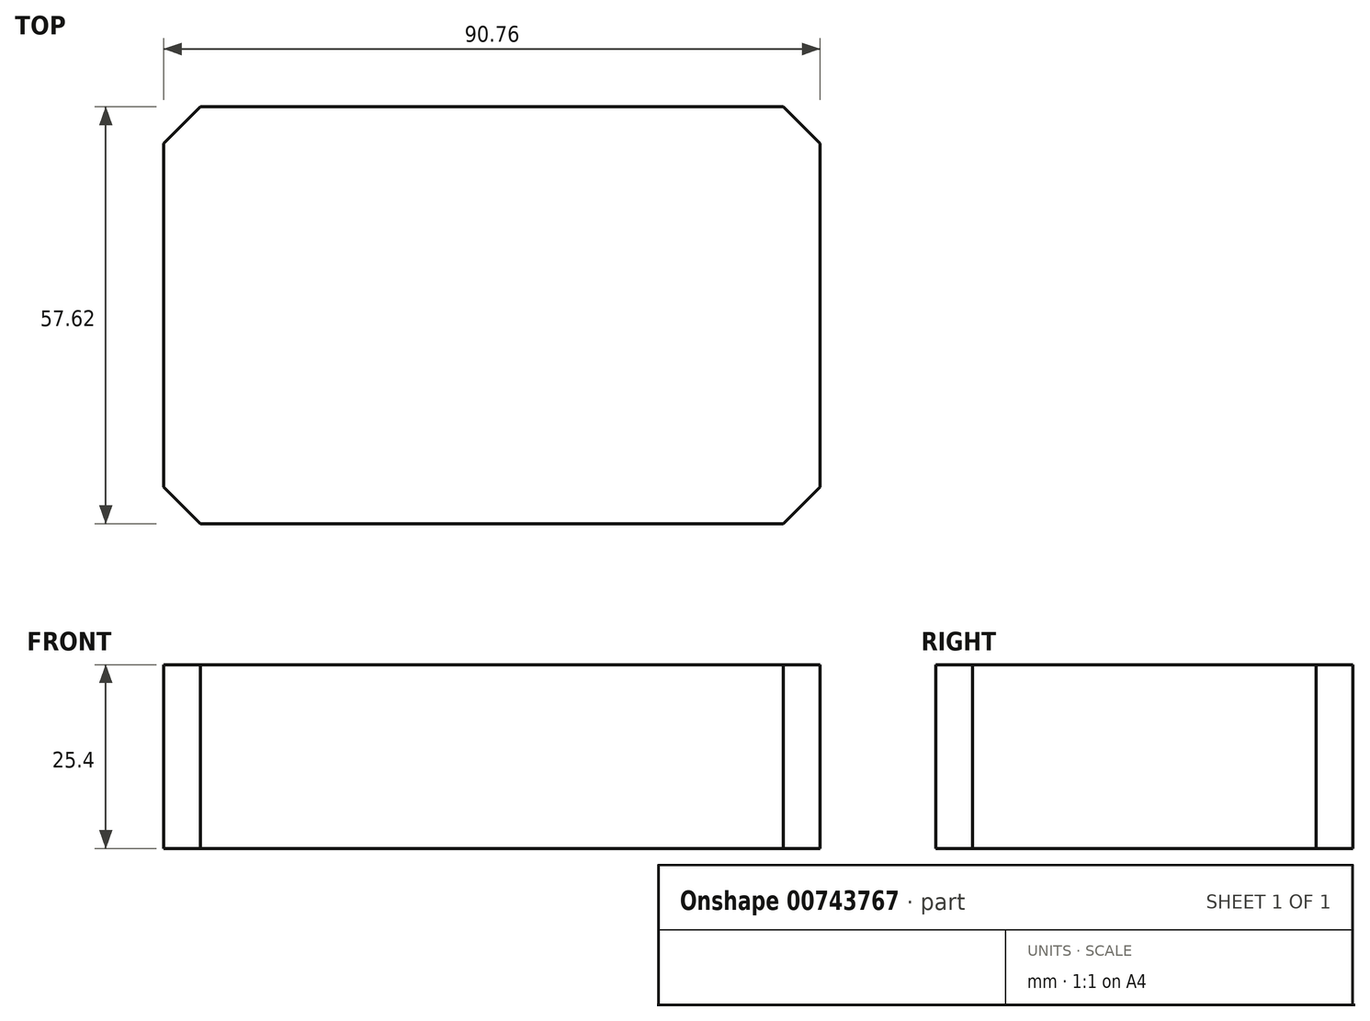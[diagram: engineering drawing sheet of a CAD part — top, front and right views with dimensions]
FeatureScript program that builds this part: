
annotation { "Feature Type Name" : "Feature", "Feature Type Description" : "" }
export const myFeature = defineFeature(function(context is Context, id is Id, definition is map)
    precondition{}
    {
        {
            var Q0;
            Q0=qCreatedBy(makeId("Top.planeOp"),FACE);
            var sketch = newSketch(context, id + "F0", { "sketchPlane" : qUnion([Q0])});
            skLineSegment(sketch, "E0.bottom", {"start": v(-45.38, 28.81) * mm, "end": v(45.38, 28.81) * mm});
            skLineSegment(sketch, "E0.top", {"start": v(-45.38, -28.81) * mm, "end": v(45.38, -28.81) * mm});
            skLineSegment(sketch, "E0.left", {"start": v(-45.38, 28.81) * mm, "end": v(-45.38, -28.81) * mm});
            skLineSegment(sketch, "E0.right", {"start": v(45.38, 28.81) * mm, "end": v(45.38, -28.81) * mm});
            skPoint(sketch, "E0.middle", {"position": v(0, 0) * mm});
            skSolve(sketch);
        }
        {
            var Q0;
            Q0=makeQuery(id+"F0.imprint","IMPRINT",FACE,{"disambiguationData":[TD([[makeQuery(id+"F0.imprint","IMPRINT",EDGE,{"derivedFrom":sQuery(id+"F0.wireOp",EDGE,"E0.bottom")}),-1.0]])]});
            extrude(context, id + "F1", {"entities" : qUnion([Q0]), "depth" : 25.4 * mm, "offsetDistance" : 25.4 * mm});
        }
        {
            var Q0;
            Q0=makeQuery(id+"F1.opExtrude","SWEPT_EDGE",EDGE,{"disambiguationData":[OSD([sQuery(id+"F0.wireOp",EDGE,"E0.top"),sQuery(id+"F0.wireOp",EDGE,"E0.right")])]});
            var Q1;
            Q1=makeQuery(id+"F1.opExtrude","SWEPT_EDGE",EDGE,{"disambiguationData":[OSD([sQuery(id+"F0.wireOp",EDGE,"E0.bottom"),sQuery(id+"F0.wireOp",EDGE,"E0.right")])]});
            var Q2;
            Q2=makeQuery(id+"F1.opExtrude","SWEPT_EDGE",EDGE,{"disambiguationData":[OSD([sQuery(id+"F0.wireOp",EDGE,"E0.top"),sQuery(id+"F0.wireOp",EDGE,"E0.left")])]});
            var Q3;
            Q3=makeQuery(id+"F1.opExtrude","SWEPT_EDGE",EDGE,{"disambiguationData":[OSD([sQuery(id+"F0.wireOp",EDGE,"E0.bottom"),sQuery(id+"F0.wireOp",EDGE,"E0.left")])]});
            chamfer(context, id + "F2", {"entities" : qUnion([Q0, Q1, Q2, Q3]), "width" : 5.08 * mm, "tangentPropagation" : true});
        }
    });
